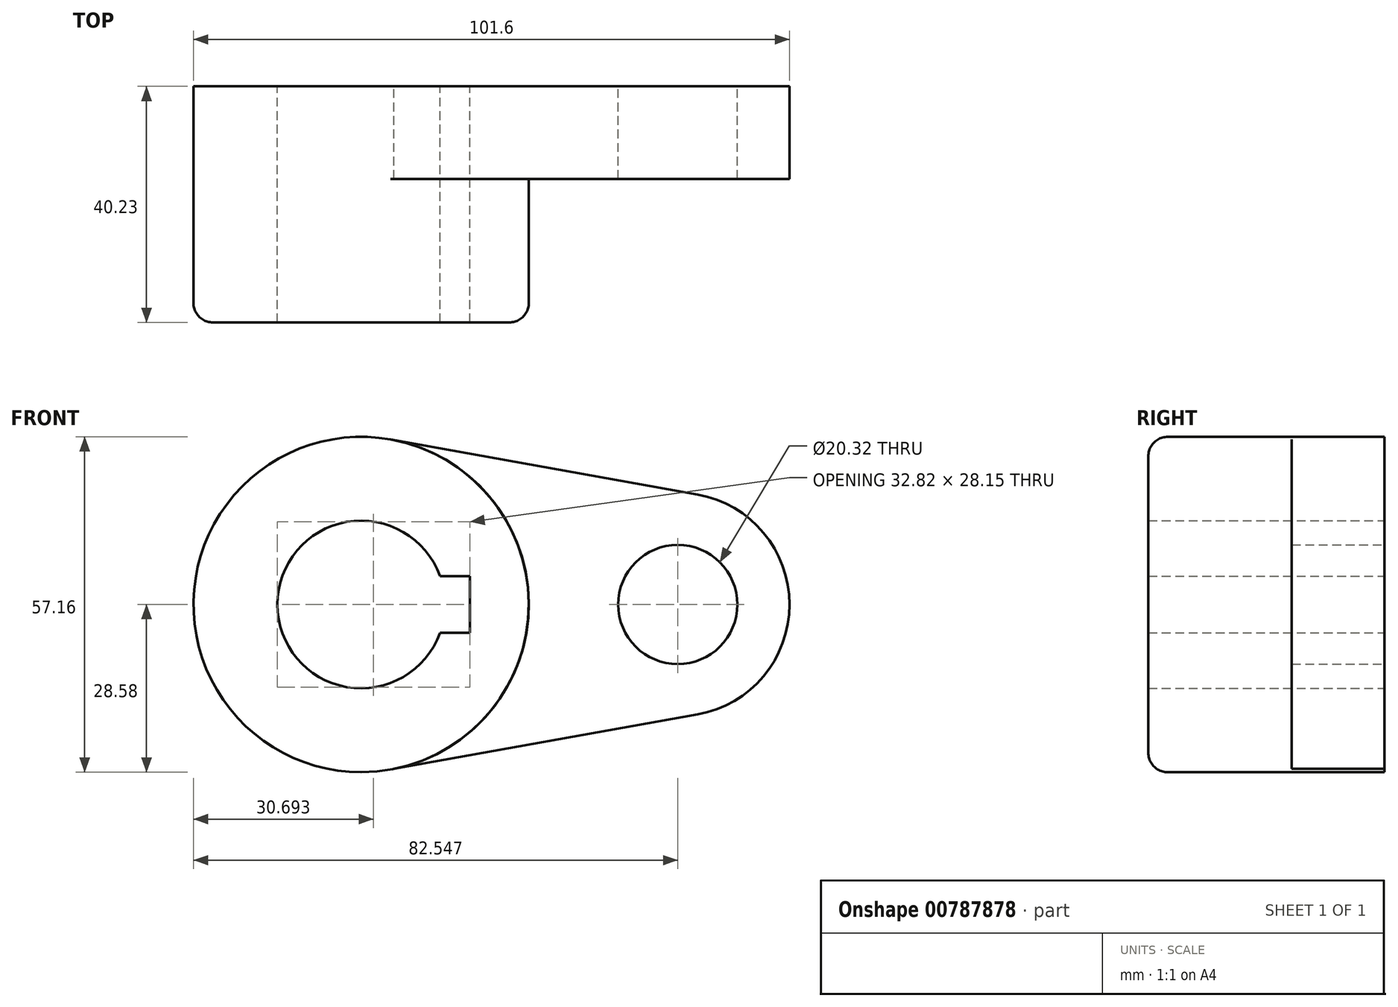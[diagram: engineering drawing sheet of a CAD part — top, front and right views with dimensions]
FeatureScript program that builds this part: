
annotation { "Feature Type Name" : "Feature", "Feature Type Description" : "" }
export const myFeature = defineFeature(function(context is Context, id is Id, definition is map)
    precondition{}
    {
        {
            var Q0;
            Q0=qCreatedBy(makeId("Front.planeOp"),FACE);
            var sketch = newSketch(context, id + "F0", { "sketchPlane" : qUnion([Q0])});
            skCircle(sketch, "E0", {"center": v(-52.82, 0) * mm, "radius": 28.58 * mm});
            skCircle(sketch, "E1", {"center": v(1.16, 0) * mm, "radius": 19.05 * mm});
            skCircle(sketch, "E2", {"center": v(1.16, 0) * mm, "radius": 10.16 * mm});
            skCircle(sketch, "E3", {"center": v(-52.82, 0) * mm, "radius": 14.29 * mm});
            skLineSegment(sketch, "E4", {"start": v(-47.78, 28.13) * mm, "end": v(4.52, 18.75) * mm});
            skLineSegment(sketch, "E5", {"start": v(-47.22, -28.02) * mm, "end": v(4.52, -18.75) * mm});
            skLineSegment(sketch, "E6", {"start": v(-39.37, 4.83) * mm, "end": v(-34.29, 4.83) * mm});
            skLineSegment(sketch, "E7", {"start": v(-34.29, 4.83) * mm, "end": v(-34.29, -4.83) * mm});
            skLineSegment(sketch, "E8", {"start": v(-34.29, -4.83) * mm, "end": v(-39.37, -4.83) * mm});
            skLineSegment(sketch, "E9", {"start": v(-52.82, 0) * mm, "end": v(-34.29, 0) * mm});
            skSolve(sketch);
        }
        {
            var Q0;
            {var subQ0=sQuery(id+"F0.wireOp",EDGE,"E6");Q0=makeQuery(id+"F0.imprint","IMPRINT",FACE,{"disambiguationData":[TD([[makeQuery(id+"F0.imprint","IMPRINT",EDGE,{"derivedFrom":subQ0}),1.0]])]});}
            extrude(context, id + "F1", {"entities" : qUnion([Q0]), "depth" : 40.23 * mm, "offsetDistance" : 25.4 * mm});
        }
        {
            var Q0;
            {var subQ0=sQuery(id+"F0.wireOp",EDGE,"E4");Q0=makeQuery(id+"F0.imprint","IMPRINT",FACE,{"disambiguationData":[TD([[makeQuery(id+"F0.imprint","IMPRINT",EDGE,{"derivedFrom":subQ0}),-1.0]])]});}
            var Q1;
            Q1=makeQuery(id+"F0.imprint","IMPRINT",FACE,{"disambiguationData":[TD([[makeQuery(id+"F0.imprint","IMPRINT",EDGE,{"derivedFrom":sQuery(id+"F0.wireOp",EDGE,"E2")}),-1.0]])]});
            extrude(context, id + "F2", {"entities" : qUnion([Q0, Q1]), "operationType" : NewBodyOperationType.ADD, "depth" : 15.77 * mm, "offsetDistance" : 25.4 * mm});
        }
        {
            var Q0;
            Q0=makeQuery(id+"F1.opExtrude","CAP_EDGE",EDGE,{"disambiguationData":[OSD([sQuery(id+"F0.wireOp",EDGE,"E0")])],"isStart":false});
            fillet(context, id + "F3", {"entities" : qUnion([Q0]), "radius" : 3.3 * mm, "tangentPropagation" : true, "allowEdgeOverflow" : false});
        }
    });
